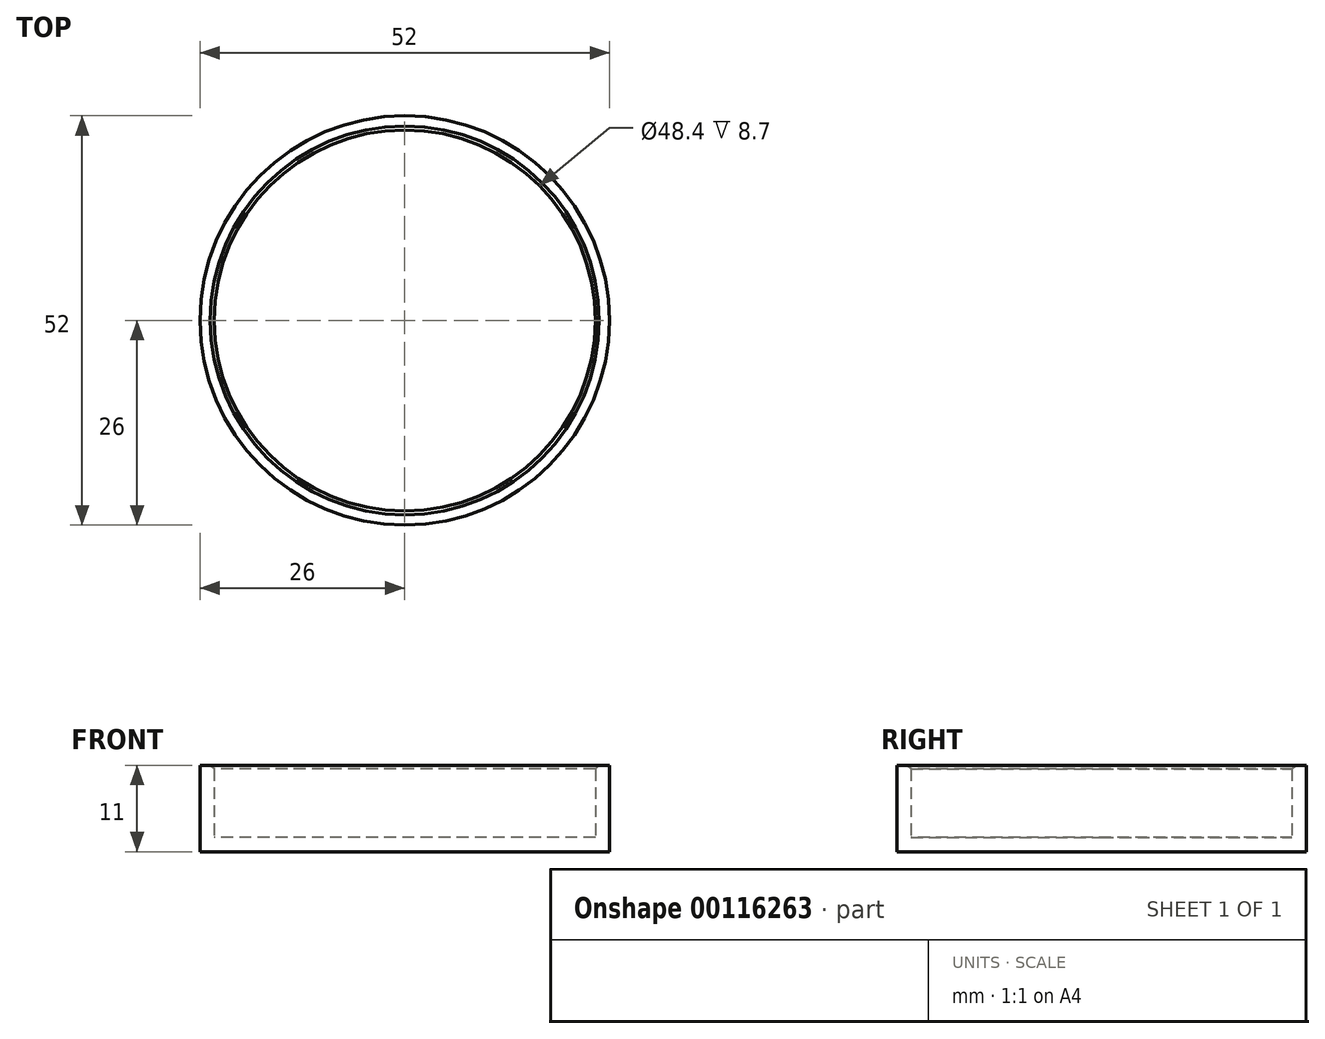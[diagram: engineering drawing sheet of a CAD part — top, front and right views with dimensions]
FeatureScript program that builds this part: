
annotation { "Feature Type Name" : "Feature", "Feature Type Description" : "" }
export const myFeature = defineFeature(function(context is Context, id is Id, definition is map)
    precondition{}
    {
        {
            var Q0;
            Q0=qCreatedBy(makeId("Top.planeOp"),FACE);
            var sketch = newSketch(context, id + "F0", { "sketchPlane" : qUnion([Q0])});
            skCircle(sketch, "E0", {"center": v(0, 0) * mm, "radius": 26 * mm});
            skSolve(sketch);
        }
        {
            var Q0;
            Q0 = qSketchRegion(id + "F0", true);
            extrude(context, id + "F1", {"entities" : qUnion([Q0]), "depth" : 11 * mm});
        }
        {
            var Q0;
            Q0=makeQuery(id+"F1.opExtrude","CAP_FACE",FACE,{"disambiguationData":[OSD([sQuery(id+"F0.wireOp",EDGE,"E0")])],"isStart":false});
            shell(context, id + "F2", {"entities" : qUnion([Q0]), "thickness" : 1.8 * mm});
        }
        {
            var Q0;
            {var subQ0=sQuery(id+"F0.wireOp",EDGE,"E0");Q0=makeQuery(id+"F2.opShell","OFFSET_EDGE",EDGE,{"disambiguationData":[OSD([subQ0]),TDD([makeQuery(id+"F1.opExtrude","CAP_EDGE",EDGE,{"disambiguationData":[OSD([subQ0])],"isStart":false})])]});}
            chamfer(context, id + "F3", {"entities" : qUnion([Q0]), "width" : 0.5 * mm, "tangentPropagation" : true});
        }
    });
